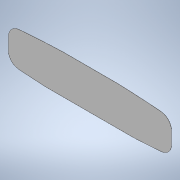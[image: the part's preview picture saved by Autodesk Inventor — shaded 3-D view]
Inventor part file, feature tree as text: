
AUTODESK INVENTOR PART (.ipt)
format: ipt  version: 2021 (Build 250183000, 183)  size: 128,000 bytes
history: native  units: mm
features: other x3, sketch x1, extrude x1
ambient origin geometry x8: Origin, YZ Plane, XZ Plane, XY Plane, X Axis, Y Axis, Z Axis, Center Point
bodies: Solid1 (feature_tree)
feature tree (5):
  other  "Blocks"
  sketch  "Sketch2"  dims[d0=600.0mm d1=200.0mm d2=143.0mm d3=200.0mm d4=20.0mm d5=42.0mm d6=40.0mm d7=40.0mm d8=42.0mm d9=10.0mm d10=140.0mm d11=10.0mm d12=140.0mm d13=120.0mm d14=120.0mm d15=75.0mm d16=300.0mm d18=0.0mm d19=0.5mm d20=200.0mm d21=320.0mm d22=13.0mm d23=13.0mm]
  other  "Block1:1"
  other  "Block1"
  extrude  "Extrusion1"  Depth=0.5mm
